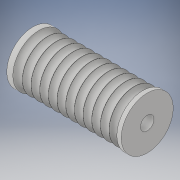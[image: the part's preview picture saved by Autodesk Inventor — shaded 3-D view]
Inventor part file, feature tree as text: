
AUTODESK INVENTOR PART (.ipt)
format: ipt  version: 2018 (Build 220112000, 112)  size: 361,984 bytes
history: native  units: in
note: dims shown in document units (in); Inventor stores cm internally (conversion verified against a paired STEP export)
features: revolve x1, sketch x1
ambient origin geometry x8: Origin, YZ Plane, XZ Plane, XY Plane, X Axis, Y Axis, Z Axis, Center Point
bodies: Body1 (feature_tree)
feature tree (2):
  revolve  "Revolution3"  [1 undecoded]
  sketch  "Sketch1"  dims[d33=0.75in d34=3.3in d35=0.125in d40=0.125in d43=0.125in d44=0.125in d46=0.125in d47=0.125in d56=0.125in d59=0.125in d60=90.0deg d63=0.125in d70=0.125in d71=0.0in d72=0.195in d73=0.125in d75=0.125in d76=0.125in d77=0.025in d78=0.175in d79=90.0deg d81=90.0deg]
note: 1 required parameter value undecoded (feature->parameter linkage not recoverable at this tier; creation-order binding heuristic only, values carry confidence <= 0.55)
